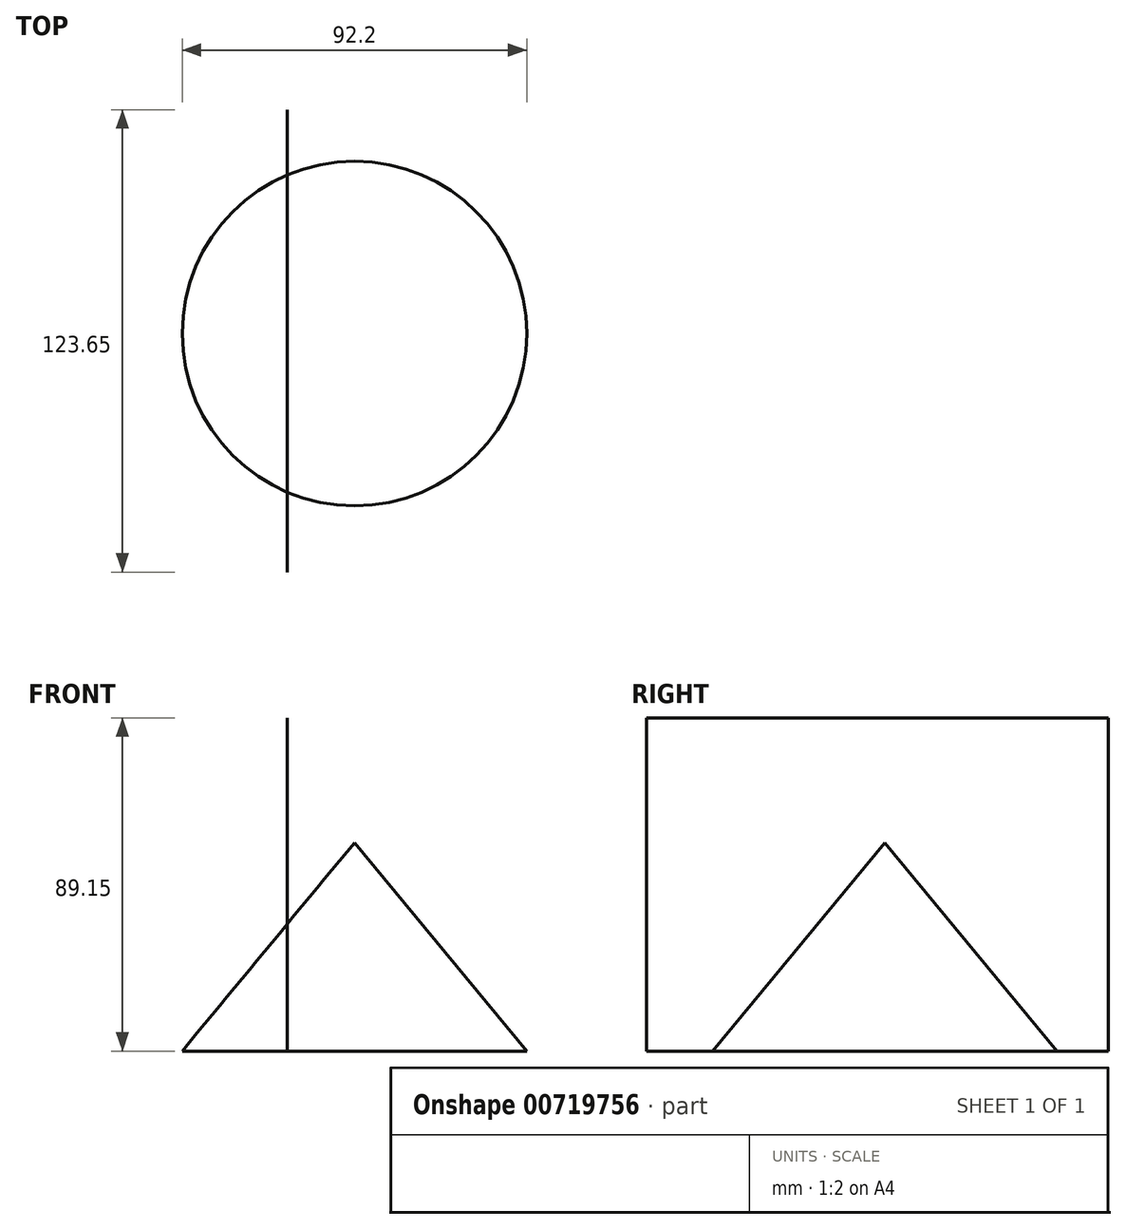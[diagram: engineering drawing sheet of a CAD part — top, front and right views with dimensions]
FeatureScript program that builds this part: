
annotation { "Feature Type Name" : "Feature", "Feature Type Description" : "" }
export const myFeature = defineFeature(function(context is Context, id is Id, definition is map)
    precondition{}
    {
        {
            var Q0;
            Q0=qCreatedBy(makeId("Front.planeOp"),FACE);
            var sketch = newSketch(context, id + "F0", { "sketchPlane" : qUnion([Q0])});
            skLineSegment(sketch, "E0", {"start": v(0, 55.73) * mm, "end": v(-46.1, 0) * mm});
            skLineSegment(sketch, "E1", {"start": v(-46.1, 0) * mm, "end": v(0, 0) * mm});
            skLineSegment(sketch, "E2", {"start": v(0, 0) * mm, "end": v(0, 55.73) * mm});
            skSolve(sketch);
        }
        {
            var Q0;
            Q0=sQuery(id+"F0.wireOp",EDGE,"E0");
            var Q1;
            Q1=sQuery(id+"F0.wireOp",EDGE,"E1");
            var Q2;
            Q2=sQuery(id+"F0.wireOp",EDGE,"E2");
            revolve(context, id + "F1", {"bodyType" : ToolBodyType.SURFACE, "surfaceOperationType" : NewSurfaceOperationType.NEW, "surfaceEntities" : qUnion([Q0, Q1]), "axis" : qUnion([Q2]), "revolveType" : RevolveType.FULL});
        }
        {
            var Q0;
            Q0=qCreatedBy(makeId("Top.planeOp"),FACE);
            var sketch = newSketch(context, id + "F2", { "sketchPlane" : qUnion([Q0])});
            skLineSegment(sketch, "E3", {"start": v(-17.99, 59.86) * mm, "end": v(-17.99, -63.8) * mm});
            skSolve(sketch);
        }
        {
            var Q0;
            Q0=sQuery(id+"F2.wireOp",EDGE,"E3");
            extrude(context, id + "F3", {"bodyType" : ToolBodyType.SURFACE, "surfaceEntities" : qUnion([Q0]), "depth" : 89.15 * mm, "offsetDistance" : 25.4 * mm});
        }
    });
